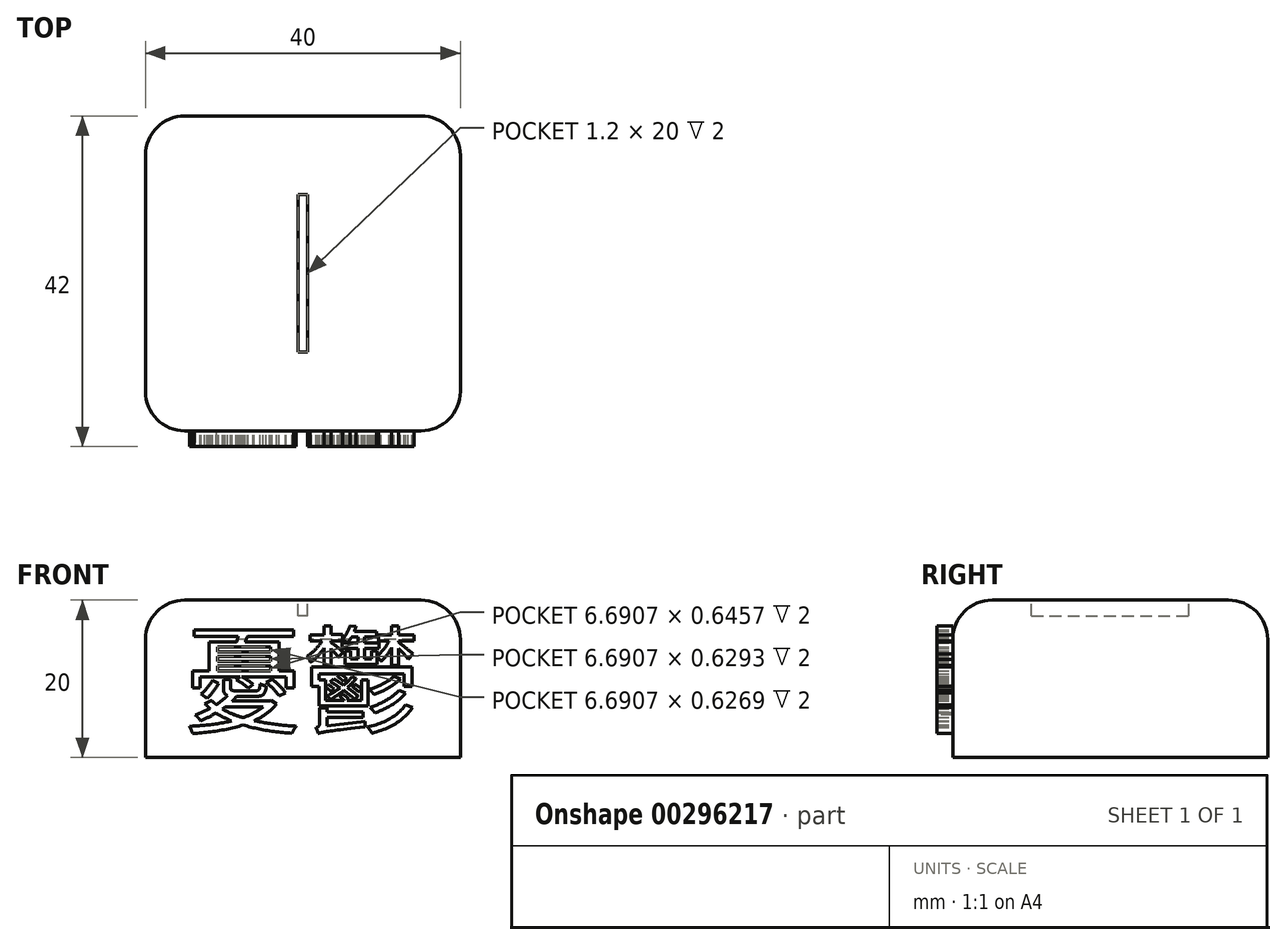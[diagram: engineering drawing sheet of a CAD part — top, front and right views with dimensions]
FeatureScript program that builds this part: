
annotation { "Feature Type Name" : "Feature", "Feature Type Description" : "" }
export const myFeature = defineFeature(function(context is Context, id is Id, definition is map)
    precondition{}
    {
        {
            var Q0;
            Q0=qCreatedBy(makeId("Top.planeOp"),FACE);
            var sketch = newSketch(context, id + "F0", { "sketchPlane" : qUnion([Q0])});
            skLineSegment(sketch, "E0.bottom", {"start": v(20, -20) * mm, "end": v(-20, -20) * mm});
            skLineSegment(sketch, "E0.top", {"start": v(20, 20) * mm, "end": v(-20, 20) * mm});
            skLineSegment(sketch, "E0.left", {"start": v(20, -20) * mm, "end": v(20, 20) * mm});
            skLineSegment(sketch, "E0.right", {"start": v(-20, -20) * mm, "end": v(-20, 20) * mm});
            skPoint(sketch, "E0.middle", {"position": v(0, 0) * mm});
            skLineSegment(sketch, "E1.bottom", {"start": v(0.6, -10) * mm, "end": v(-0.6, -10) * mm});
            skLineSegment(sketch, "E1.top", {"start": v(0.6, 10) * mm, "end": v(-0.6, 10) * mm});
            skLineSegment(sketch, "E1.left", {"start": v(0.6, -10) * mm, "end": v(0.6, 10) * mm});
            skLineSegment(sketch, "E1.right", {"start": v(-0.6, -10) * mm, "end": v(-0.6, 10) * mm});
            skSolve(sketch);
        }
        {
            var Q0;
            Q0=makeQuery(id+"F0.imprint","IMPRINT",FACE,{"disambiguationData":[TD([[makeQuery(id+"F0.imprint","IMPRINT",EDGE,{"derivedFrom":sQuery(id+"F0.wireOp",EDGE,"E0.bottom")}),-1.0]])]});
            var Q1;
            Q1=makeQuery(id+"F0.imprint","IMPRINT",FACE,{"disambiguationData":[TD([[makeQuery(id+"F0.imprint","IMPRINT",EDGE,{"derivedFrom":sQuery(id+"F0.wireOp",EDGE,"E1.bottom")}),-1.0]])]});
            extrude(context, id + "F1", {"entities" : qUnion([Q0, Q1]), "oppositeDirection" : true, "depth" : 20 * mm});
        }
        {
            var Q0;
            Q0=makeQuery(id+"F0.imprint","IMPRINT",FACE,{"disambiguationData":[TD([[makeQuery(id+"F0.imprint","IMPRINT",EDGE,{"derivedFrom":sQuery(id+"F0.wireOp",EDGE,"E1.bottom")}),-1.0]])]});
            extrude(context, id + "F2", {"entities" : qUnion([Q0]), "operationType" : NewBodyOperationType.REMOVE, "oppositeDirection" : true, "depth" : 2 * mm});
        }
        {
            var Q0;
            Q0=makeQuery(id+"F2.boolean.opBoolean","COPY",EDGE,{"derivedFrom":makeQuery(id+"F2.opExtrude","CAP_EDGE",EDGE,{"disambiguationData":[OSD([sQuery(id+"F0.wireOp",EDGE,"E1.left")])],"isStart":true})});
            var Q1;
            Q1=makeQuery(id+"F2.boolean.opBoolean","COPY",EDGE,{"derivedFrom":makeQuery(id+"F2.opExtrude","CAP_EDGE",EDGE,{"disambiguationData":[OSD([sQuery(id+"F0.wireOp",EDGE,"E1.right")])],"isStart":true})});
            var Q2;
            Q2=makeQuery(id+"F1.opExtrude","SWEPT_EDGE",EDGE,{"disambiguationData":[OSD([sQuery(id+"F0.wireOp",EDGE,"E0.bottom"),sQuery(id+"F0.wireOp",EDGE,"E0.left")])]});
            var Q3;
            Q3=makeQuery(id+"F1.opExtrude","SWEPT_EDGE",EDGE,{"disambiguationData":[OSD([sQuery(id+"F0.wireOp",EDGE,"E0.top"),sQuery(id+"F0.wireOp",EDGE,"E0.left")])]});
            var Q4;
            Q4=makeQuery(id+"F1.opExtrude","CAP_EDGE",EDGE,{"disambiguationData":[OSD([sQuery(id+"F0.wireOp",EDGE,"E0.left")])],"isStart":true});
            var Q5;
            Q5=makeQuery(id+"F1.opExtrude","SWEPT_EDGE",EDGE,{"disambiguationData":[OSD([sQuery(id+"F0.wireOp",EDGE,"E0.bottom"),sQuery(id+"F0.wireOp",EDGE,"E0.right")])]});
            var Q6;
            Q6=makeQuery(id+"F1.opExtrude","SWEPT_EDGE",EDGE,{"disambiguationData":[OSD([sQuery(id+"F0.wireOp",EDGE,"E0.top"),sQuery(id+"F0.wireOp",EDGE,"E0.right")])]});
            var Q7;
            Q7=makeQuery(id+"F1.opExtrude","CAP_EDGE",EDGE,{"disambiguationData":[OSD([sQuery(id+"F0.wireOp",EDGE,"E0.top")])],"isStart":true});
            var Q8;
            Q8=makeQuery(id+"F1.opExtrude","CAP_EDGE",EDGE,{"disambiguationData":[OSD([sQuery(id+"F0.wireOp",EDGE,"E0.right")])],"isStart":true});
            var Q9;
            Q9=makeQuery(id+"F1.opExtrude","CAP_EDGE",EDGE,{"disambiguationData":[OSD([sQuery(id+"F0.wireOp",EDGE,"E0.bottom")])],"isStart":true});
            fillet(context, id + "F3", {"entities" : qUnion([Q0, Q1, Q2, Q3, Q4, Q5, Q6, Q7, Q8, Q9]), "radius" : 5 * mm, "tangentPropagation" : true, "allowEdgeOverflow" : false});
        }
        {
            var Q0;
            Q0=makeQuery(id+"F1.opExtrude","SWEPT_FACE",FACE,{"disambiguationData":[OSD([sQuery(id+"F0.wireOp",EDGE,"E0.bottom")])]});
            var sketch = newSketch(context, id + "F4", { "sketchPlane" : qUnion([Q0])});
            skText(sketch, "E2", { "text": "憂鬱", "fontName": "NotoSansCJKtc-Regular.otf"});
            const initialGuessF4  = {"E2": [-0.015, -0.01578, 1, 0, 0.01078]};
            skSetInitialGuess(sketch, initialGuessF4);
            skSolve(sketch);
        }
        {
            var Q0;
            Q0=makeQuery(id+"F4.imprint","IMPRINT",FACE,{"disambiguationData":[TD([[makeQuery(id+"F4.imprint","IMPRINT",EDGE,{"derivedFrom":sQuery(id+"F4.wireOp",EDGE,"E2.sketch_text.stroke-133")}),1.0]])]});
            var Q1;
            Q1=makeQuery(id+"F4.imprint","IMPRINT",FACE,{"disambiguationData":[TD([[makeQuery(id+"F4.imprint","IMPRINT",EDGE,{"derivedFrom":sQuery(id+"F4.wireOp",EDGE,"E2.sketch_text.stroke-86")}),1.0]])]});
            var Q2;
            Q2=makeQuery(id+"F4.imprint","IMPRINT",FACE,{"disambiguationData":[TD([[makeQuery(id+"F4.imprint","IMPRINT",EDGE,{"derivedFrom":sQuery(id+"F4.wireOp",EDGE,"E2.sketch_text.stroke-117")}),1.0]])]});
            var Q3;
            Q3=makeQuery(id+"F4.imprint","IMPRINT",FACE,{"disambiguationData":[TD([[makeQuery(id+"F4.imprint","IMPRINT",EDGE,{"derivedFrom":sQuery(id+"F4.wireOp",EDGE,"E2.sketch_text.stroke-129")}),1.0]])]});
            var Q4;
            Q4=makeQuery(id+"F4.imprint","IMPRINT",FACE,{"disambiguationData":[TD([[makeQuery(id+"F4.imprint","IMPRINT",EDGE,{"derivedFrom":sQuery(id+"F4.wireOp",EDGE,"E2.sketch_text.stroke-82")}),1.0]])]});
            var Q5;
            Q5=makeQuery(id+"F4.imprint","IMPRINT",FACE,{"disambiguationData":[TD([[makeQuery(id+"F4.imprint","IMPRINT",EDGE,{"derivedFrom":sQuery(id+"F4.wireOp",EDGE,"E2.sketch_text.stroke-78")}),1.0]])]});
            var Q6;
            Q6=makeQuery(id+"F4.imprint","IMPRINT",FACE,{"disambiguationData":[TD([[makeQuery(id+"F4.imprint","IMPRINT",EDGE,{"derivedFrom":sQuery(id+"F4.wireOp",EDGE,"E2.sketch_text.stroke-145")}),1.0]])]});
            var Q7;
            {var subQ7=sQuery(id+"F4.wireOp",EDGE,"E2.sketch_text.stroke-167");Q7=makeQuery(id+"F4.imprint","IMPRINT",FACE,{"disambiguationData":[TD([[makeQuery(id+"F4.imprint","IMPRINT",EDGE,{"derivedFrom":subQ7}),1.0]])]});}
            var Q8;
            {var subQ0=sQuery(id+"F4.wireOp",EDGE,"E2.sketch_text.stroke-150");Q8=makeQuery(id+"F4.imprint","IMPRINT",FACE,{"disambiguationData":[TD([[makeQuery(id+"F4.imprint","IMPRINT",EDGE,{"derivedFrom":subQ0}),1.0]])]});}
            var Q9;
            {var subQ8=sQuery(id+"F4.wireOp",EDGE,"E2.sketch_text.stroke-156");Q9=makeQuery(id+"F4.imprint","IMPRINT",FACE,{"disambiguationData":[TD([[makeQuery(id+"F4.imprint","IMPRINT",EDGE,{"derivedFrom":subQ8}),1.0]])]});}
            var Q10;
            {var subQ6=sQuery(id+"F4.wireOp",EDGE,"E2.sketch_text.stroke-180");Q10=makeQuery(id+"F4.imprint","IMPRINT",FACE,{"disambiguationData":[TD([[makeQuery(id+"F4.imprint","IMPRINT",EDGE,{"derivedFrom":subQ6}),1.0]])]});}
            var Q11;
            {var subQ0=sQuery(id+"F4.wireOp",EDGE,"E2.sketch_text.stroke-25");Q11=makeQuery(id+"F4.imprint","IMPRINT",FACE,{"disambiguationData":[TD([[makeQuery(id+"F4.imprint","IMPRINT",EDGE,{"derivedFrom":subQ0}),1.0]])]});}
            var Q12;
            Q12=makeQuery(id+"F4.imprint","IMPRINT",FACE,{"disambiguationData":[TD([[makeQuery(id+"F4.imprint","IMPRINT",EDGE,{"derivedFrom":sQuery(id+"F4.wireOp",EDGE,"E2.sketch_text.stroke-0")}),1.0]])]});
            var Q13;
            Q13=makeQuery(id+"F4.imprint","IMPRINT",FACE,{"disambiguationData":[TD([[makeQuery(id+"F4.imprint","IMPRINT",EDGE,{"derivedFrom":sQuery(id+"F4.wireOp",EDGE,"E2.sketch_text.stroke-45")}),1.0]])]});
            var Q14;
            Q14=makeQuery(id+"F4.imprint","IMPRINT",FACE,{"disambiguationData":[TD([[makeQuery(id+"F4.imprint","IMPRINT",EDGE,{"derivedFrom":sQuery(id+"F4.wireOp",EDGE,"E2.sketch_text.stroke-41")}),1.0]])]});
            var Q15;
            Q15=makeQuery(id+"F4.imprint","IMPRINT",FACE,{"disambiguationData":[TD([[makeQuery(id+"F4.imprint","IMPRINT",EDGE,{"derivedFrom":sQuery(id+"F4.wireOp",EDGE,"E2.sketch_text.stroke-37")}),1.0]])]});
            extrude(context, id + "F5", {"entities" : qUnion([Q0, Q1, Q2, Q3, Q4, Q5, Q6, Q7, Q8, Q9, Q10, Q11, Q12, Q13, Q14, Q15]), "operationType" : NewBodyOperationType.ADD, "depth" : 2 * mm});
        }
    });
